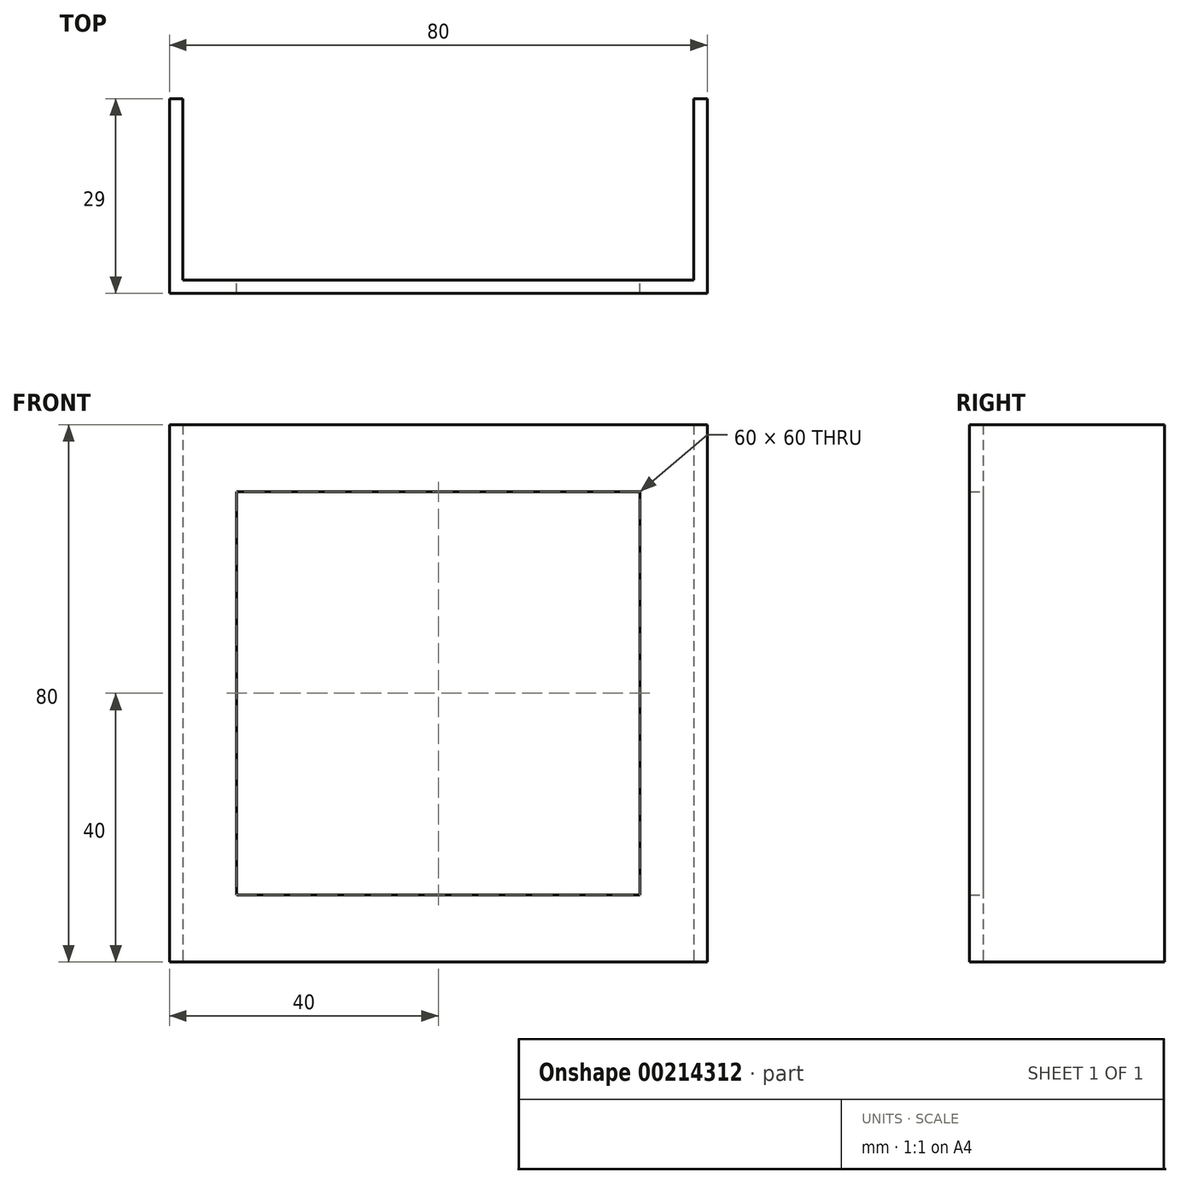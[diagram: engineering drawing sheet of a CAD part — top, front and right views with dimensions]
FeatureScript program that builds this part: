
annotation { "Feature Type Name" : "Feature", "Feature Type Description" : "" }
export const myFeature = defineFeature(function(context is Context, id is Id, definition is map)
    precondition{}
    {
        {
            var Q0;
            Q0=qCreatedBy(makeId("Front.planeOp"),FACE);
            var sketch = newSketch(context, id + "F0", { "sketchPlane" : qUnion([Q0])});
            skLineSegment(sketch, "E0.bottom", {"start": v(40, 40) * mm, "end": v(-40, 40) * mm});
            skLineSegment(sketch, "E0.top", {"start": v(40, -40) * mm, "end": v(-40, -40) * mm});
            skLineSegment(sketch, "E0.left", {"start": v(40, 40) * mm, "end": v(40, -40) * mm});
            skLineSegment(sketch, "E0.right", {"start": v(-40, 40) * mm, "end": v(-40, -40) * mm});
            skPoint(sketch, "E0.middle", {"position": v(0, 0) * mm});
            skLineSegment(sketch, "E1.bottom", {"start": v(30, 30) * mm, "end": v(-30, 30) * mm});
            skLineSegment(sketch, "E1.top", {"start": v(30, -30) * mm, "end": v(-30, -30) * mm});
            skLineSegment(sketch, "E1.left", {"start": v(30, 30) * mm, "end": v(30, -30) * mm});
            skLineSegment(sketch, "E1.right", {"start": v(-30, 30) * mm, "end": v(-30, -30) * mm});
            skSolve(sketch);
        }
        {
            var Q0;
            Q0 = qSketchRegion(id + "F0", true);
            extrude(context, id + "F1", {"entities" : qUnion([Q0]), "depth" : 2 * mm});
        }
        {
            var Q0;
            Q0=makeQuery(id+"F1.opExtrude","CAP_FACE",FACE,{"disambiguationData":[OSD([sQuery(id+"F0.wireOp",EDGE,"E0.bottom"),sQuery(id+"F0.wireOp",EDGE,"E0.top"),sQuery(id+"F0.wireOp",EDGE,"E0.left"),sQuery(id+"F0.wireOp",EDGE,"E0.right"),sQuery(id+"F0.wireOp",EDGE,"E1.bottom"),sQuery(id+"F0.wireOp",EDGE,"E1.top"),sQuery(id+"F0.wireOp",EDGE,"E1.left"),sQuery(id+"F0.wireOp",EDGE,"E1.right")])],"isStart":true});
            var sketch = newSketch(context, id + "F2", { "sketchPlane" : qUnion([Q0])});
            skLineSegment(sketch, "E2.bottom", {"start": v(-40, 40) * mm, "end": v(-38, 40) * mm});
            skLineSegment(sketch, "E2.top", {"start": v(-40, -40) * mm, "end": v(-38, -40) * mm});
            skLineSegment(sketch, "E2.left", {"start": v(-40, 40) * mm, "end": v(-40, -40) * mm});
            skLineSegment(sketch, "E2.right", {"start": v(-38, 40) * mm, "end": v(-38, -40) * mm});
            skLineSegment(sketch, "E3.bottom", {"start": v(40, 40) * mm, "end": v(38, 40) * mm});
            skLineSegment(sketch, "E3.top", {"start": v(40, -40) * mm, "end": v(38, -40) * mm});
            skLineSegment(sketch, "E3.left", {"start": v(40, 40) * mm, "end": v(40, -40) * mm});
            skLineSegment(sketch, "E3.right", {"start": v(38, 40) * mm, "end": v(38, -40) * mm});
            skSolve(sketch);
        }
        {
            var Q0;
            Q0 = qSketchRegion(id + "F2", true);
            extrude(context, id + "F3", {"entities" : qUnion([Q0]), "operationType" : NewBodyOperationType.ADD, "depth" : 27 * mm});
        }
    });
